# Revit family: Alcon-14124-4-Revit-Family
name_source: partatom
category: Lighting Fixtures
units: mm (PartAtom-declared; Revit-internal decimal feet)

## family parameters
Always vertical = Yes
Cut with Voids When Loaded = No
Host = Ceiling
Light Source = Yes
OmniClass Number = 23.80.70.11
OmniClass Title = Luminaries for Internal Lighting
Part Type = Normal
Room Calculation Point = No
Round Connector Dimension = Use Diameter
Shared = No

## types (1)
- Type 1
    Color Filter = 16777215
    Default Elevation = 0' - 0"
    Dimming Lamp Color Temperature Shift = <None>
    Housing = <By Category>
    Lens = <By Category>
    Light Source Symbol Length = 10' - 0"
    LightSource = <By Category>
    Link To Product Page = https://www.alconlighting.com
    Manufacturer = Alcon Light
    Product Identity = Alcon Lighting 14124-4
    Spot Beam Angle = 30.00°
    Spot Field Angle = 90.00°
    Tilt Angle = 60.00°

## geometry (parser evidence)
native form markers: Sweep x2
no freeform markers — native parametric forms only
